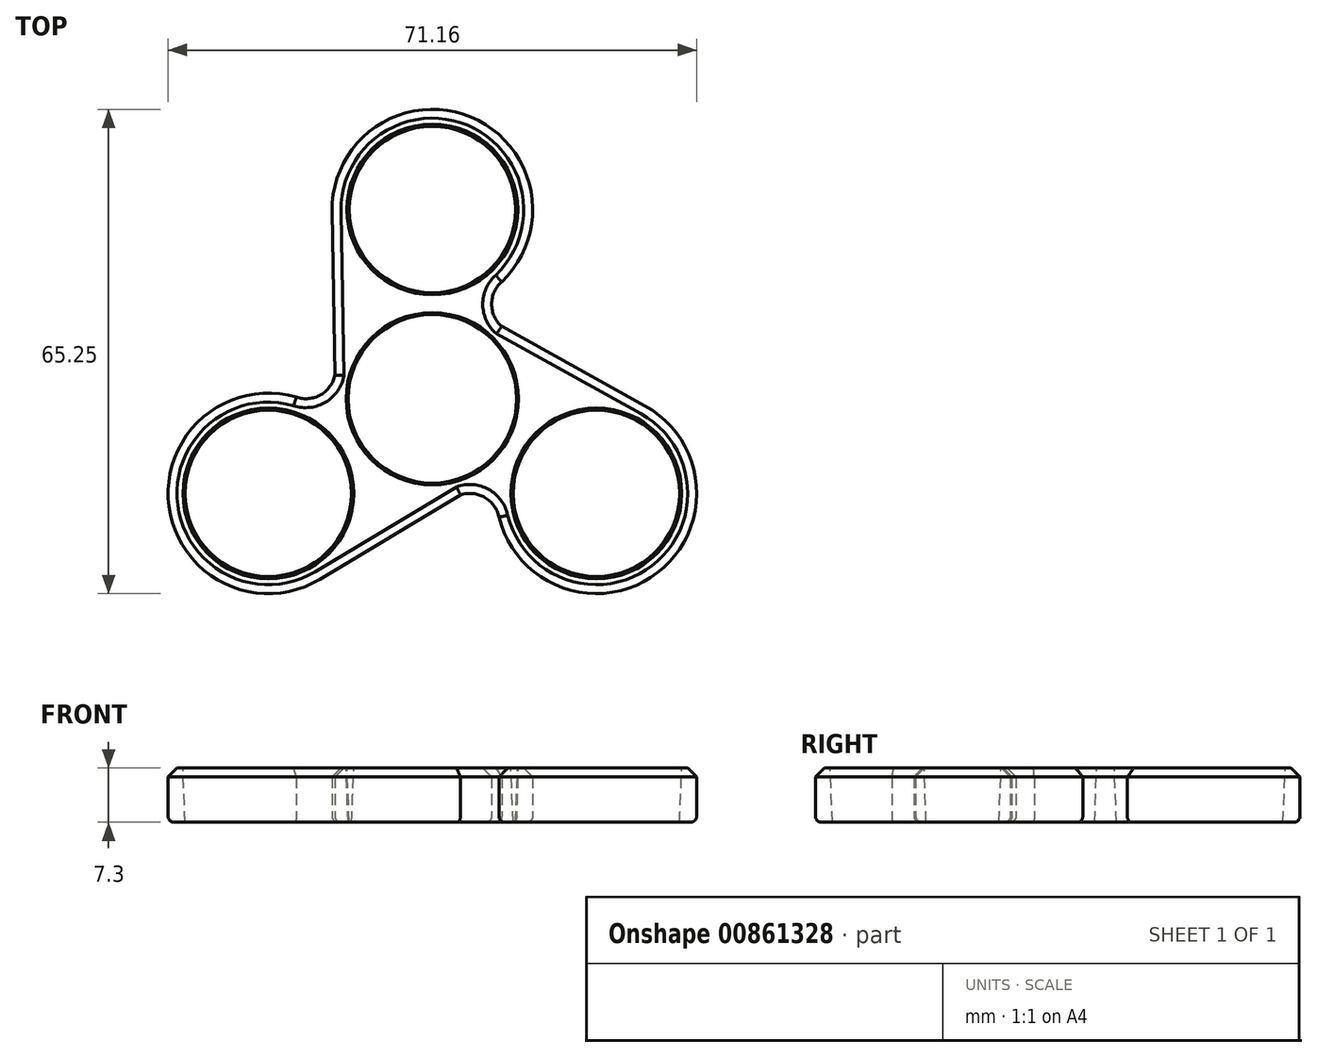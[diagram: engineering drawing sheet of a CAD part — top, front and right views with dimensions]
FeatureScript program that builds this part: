
annotation { "Feature Type Name" : "Feature", "Feature Type Description" : "" }
export const myFeature = defineFeature(function(context is Context, id is Id, definition is map)
    precondition{}
    {
        {
            var Q0;
            Q0=qCreatedBy(makeId("Top.planeOp"),FACE);
            var sketch = newSketch(context, id + "F0", { "sketchPlane" : qUnion([Q0])});
            skCircle(sketch, "E0", {"center": v(0, 0) * mm, "radius": 13.5 * mm});
            skCircle(sketch, "E1", {"center": v(0, 25.5) * mm, "radius": 13.5 * mm});
            skLineSegment(sketch, "E2.bottom", {"start": v(0, 9.75) * mm, "end": v(9.34, 9.75) * mm});
            skLineSegment(sketch, "E2.top", {"start": v(0, 15.75) * mm, "end": v(9.34, 15.75) * mm});
            skLineSegment(sketch, "E2.left", {"start": v(0, 9.75) * mm, "end": v(0, 15.75) * mm});
            skLineSegment(sketch, "E2.right", {"start": v(9.34, 9.75) * mm, "end": v(9.34, 15.75) * mm});
            skArc(sketch, "E3", {"start": v(9.34, 15.75) * mm, "mid": v(7.98, 12.75) * mm, "end": v(9.34, 9.75) * mm});
            skArc(sketch, "E4.1.0", {"start": v(-18.3, 0.21) * mm, "mid": v(-15.03, 0.54) * mm, "end": v(-13.11, 3.21) * mm});
            skCircle(sketch, "E4.1.1", {"center": v(-22.08, -12.75) * mm, "radius": 13.5 * mm});
            skArc(sketch, "E4.2.0", {"start": v(8.97, -15.96) * mm, "mid": v(7.05, -13.29) * mm, "end": v(3.78, -12.96) * mm});
            skCircle(sketch, "E4.2.1", {"center": v(22.08, -12.75) * mm, "radius": 13.5 * mm});
            skLineSegment(sketch, "E5", {"start": v(9.34, 9.75) * mm, "end": v(28.63, -0.94) * mm});
            skLineSegment(sketch, "E6.1.0", {"start": v(-13.11, 3.21) * mm, "end": v(-13.5, 25.26) * mm});
            skLineSegment(sketch, "E6.2.0", {"start": v(3.78, -12.96) * mm, "end": v(-15.13, -24.32) * mm});
            skSolve(sketch);
        }
        {
            var Q0;
            {var subQ0=sQuery(id+"F0.wireOp",EDGE,"E2.top");Q0=makeQuery(id+"F0.imprint","IMPRINT",FACE,{"disambiguationData":[TD([[makeQuery(id+"F0.imprint","IMPRINT",EDGE,{"derivedFrom":subQ0}),1.0]])]});}
            var Q1;
            {var subQ0=sQuery(id+"F0.wireOp",EDGE,"E6.1.0");Q1=makeQuery(id+"F0.imprint","IMPRINT",FACE,{"disambiguationData":[TD([[makeQuery(id+"F0.imprint","IMPRINT",EDGE,{"derivedFrom":subQ0}),-1.0]])]});}
            var Q2;
            {var subQ1=sQuery(id+"F0.wireOp",EDGE,"E2.top");Q2=makeQuery(id+"F0.imprint","IMPRINT",FACE,{"disambiguationData":[TD([[makeQuery(id+"F0.imprint","IMPRINT",EDGE,{"derivedFrom":subQ1}),-1.0]])]});}
            var Q3;
            {var subQ0=sQuery(id+"F0.wireOp",EDGE,"E1");var subQ1=sQuery(id+"F0.wireOp",EDGE,"E0");var subQ2=makeQuery(id+"F0.imprint","INTERSECT",VERTEX,{"disambiguationData":[OD(0.0)],"derivedFrom":[subQ1,subQ0]});Q3=makeQuery(id+"F0.imprint","IMPRINT",FACE,{"disambiguationData":[TD([[makeQuery(id+"F0.imprint","IMPRINT",EDGE,{"disambiguationData":[TD([[subQ2,-1.0]])],"derivedFrom":subQ1}),1.0]])]});}
            var Q4;
            {var subQ0=sQuery(id+"F0.wireOp",EDGE,"E2.left");var subQ1=sQuery(id+"F0.wireOp",EDGE,"E0");var subQ2=makeQuery(id+"F0.imprint","INTERSECT",VERTEX,{"derivedFrom":[subQ1,subQ0]});Q4=makeQuery(id+"F0.imprint","IMPRINT",FACE,{"disambiguationData":[TD([[makeQuery(id+"F0.imprint","IMPRINT",EDGE,{"disambiguationData":[TD([[subQ2,-1.0]])],"derivedFrom":subQ1}),1.0]])]});}
            var Q5;
            {var subQ5=sQuery(id+"F0.wireOp",EDGE,"E2.bottom");Q5=makeQuery(id+"F0.imprint","IMPRINT",FACE,{"disambiguationData":[TD([[makeQuery(id+"F0.imprint","IMPRINT",EDGE,{"derivedFrom":subQ5}),-1.0]])]});}
            var Q6;
            {var subQ0=sQuery(id+"F0.wireOp",EDGE,"E3");var subQ1=sQuery(id+"F0.wireOp",EDGE,"E0");var subQ2=makeQuery(id+"F0.imprint","INTERSECT",VERTEX,{"derivedFrom":[subQ1,subQ0]});Q6=makeQuery(id+"F0.imprint","IMPRINT",FACE,{"disambiguationData":[TD([[makeQuery(id+"F0.imprint","IMPRINT",EDGE,{"disambiguationData":[TD([[subQ2,-1.0]])],"derivedFrom":subQ1}),-1.0]])]});}
            var Q7;
            {var subQ0=sQuery(id+"F0.wireOp",EDGE,"E2.bottom");Q7=makeQuery(id+"F0.imprint","IMPRINT",FACE,{"disambiguationData":[TD([[makeQuery(id+"F0.imprint","IMPRINT",EDGE,{"derivedFrom":subQ0}),1.0]])]});}
            var Q8;
            {var subQ0=sQuery(id+"F0.wireOp",EDGE,"E4.2.1");var subQ1=sQuery(id+"F0.wireOp",EDGE,"E0");var subQ2=makeQuery(id+"F0.imprint","INTERSECT",VERTEX,{"disambiguationData":[OD(0.0)],"derivedFrom":[subQ1,subQ0]});Q8=makeQuery(id+"F0.imprint","IMPRINT",FACE,{"disambiguationData":[TD([[makeQuery(id+"F0.imprint","IMPRINT",EDGE,{"disambiguationData":[TD([[subQ2,-1.0]])],"derivedFrom":subQ1}),1.0]])]});}
            var Q9;
            {var subQ0=sQuery(id+"F0.wireOp",EDGE,"E4.2.0");var subQ1=sQuery(id+"F0.wireOp",EDGE,"E0");var subQ2=makeQuery(id+"F0.imprint","INTERSECT",VERTEX,{"derivedFrom":[subQ1,subQ0]});Q9=makeQuery(id+"F0.imprint","IMPRINT",FACE,{"disambiguationData":[TD([[makeQuery(id+"F0.imprint","IMPRINT",EDGE,{"disambiguationData":[TD([[subQ2,-1.0]])],"derivedFrom":subQ1}),-1.0]])]});}
            var Q10;
            {var subQ0=sQuery(id+"F0.wireOp",EDGE,"E6.2.0");Q10=makeQuery(id+"F0.imprint","IMPRINT",FACE,{"disambiguationData":[TD([[makeQuery(id+"F0.imprint","IMPRINT",EDGE,{"derivedFrom":subQ0}),-1.0]])]});}
            var Q11;
            {var subQ0=sQuery(id+"F0.wireOp",EDGE,"E4.1.1");var subQ1=sQuery(id+"F0.wireOp",EDGE,"E0");var subQ2=makeQuery(id+"F0.imprint","INTERSECT",VERTEX,{"disambiguationData":[OD(0.0)],"derivedFrom":[subQ1,subQ0]});Q11=makeQuery(id+"F0.imprint","IMPRINT",FACE,{"disambiguationData":[TD([[makeQuery(id+"F0.imprint","IMPRINT",EDGE,{"disambiguationData":[TD([[subQ2,-1.0]])],"derivedFrom":subQ1}),1.0]])]});}
            var Q12;
            {var subQ0=sQuery(id+"F0.wireOp",EDGE,"E4.1.0");var subQ1=sQuery(id+"F0.wireOp",EDGE,"E0");var subQ2=makeQuery(id+"F0.imprint","INTERSECT",VERTEX,{"derivedFrom":[subQ1,subQ0]});Q12=makeQuery(id+"F0.imprint","IMPRINT",FACE,{"disambiguationData":[TD([[makeQuery(id+"F0.imprint","IMPRINT",EDGE,{"disambiguationData":[TD([[subQ2,-1.0]])],"derivedFrom":subQ1}),-1.0]])]});}
            var Q13;
            {var subQ0=sQuery(id+"F0.wireOp",EDGE,"E4.1.1");var subQ2=sQuery(id+"F0.wireOp",EDGE,"E0");var subQ6=makeQuery(id+"F0.imprint","INTERSECT",VERTEX,{"disambiguationData":[OD(0.0)],"derivedFrom":[subQ2,subQ0]});Q13=makeQuery(id+"F0.imprint","IMPRINT",FACE,{"disambiguationData":[TD([[makeQuery(id+"F0.imprint","IMPRINT",EDGE,{"disambiguationData":[TD([[subQ6,-1.0]])],"derivedFrom":subQ2}),-1.0]])]});}
            var Q14;
            {var subQ0=sQuery(id+"F0.wireOp",EDGE,"E4.2.1");var subQ2=sQuery(id+"F0.wireOp",EDGE,"E0");var subQ6=makeQuery(id+"F0.imprint","INTERSECT",VERTEX,{"disambiguationData":[OD(0.0)],"derivedFrom":[subQ2,subQ0]});Q14=makeQuery(id+"F0.imprint","IMPRINT",FACE,{"disambiguationData":[TD([[makeQuery(id+"F0.imprint","IMPRINT",EDGE,{"disambiguationData":[TD([[subQ6,-1.0]])],"derivedFrom":subQ2}),-1.0]])]});}
            var Q15;
            {var subQ0=sQuery(id+"F0.wireOp",EDGE,"E5");Q15=makeQuery(id+"F0.imprint","IMPRINT",FACE,{"disambiguationData":[TD([[makeQuery(id+"F0.imprint","IMPRINT",EDGE,{"derivedFrom":subQ0}),-1.0]])]});}
            extrude(context, id + "F1", {"entities" : qUnion([Q0, Q1, Q2, Q3, Q4, Q5, Q6, Q7, Q8, Q9, Q10, Q11, Q12, Q13, Q14, Q15]), "depth" : 7.3 * mm, "offsetDistance" : 25 * mm});
        }
        {
            var Q0;
            Q0=makeQuery(id+"F1.opExtrude","CAP_FACE",FACE,{"disambiguationData":[OSD([sQuery(id+"F0.wireOp",EDGE,"E1"),sQuery(id+"F0.wireOp",EDGE,"E3"),sQuery(id+"F0.wireOp",EDGE,"E4.1.0"),sQuery(id+"F0.wireOp",EDGE,"E4.1.1"),sQuery(id+"F0.wireOp",EDGE,"E4.2.0"),sQuery(id+"F0.wireOp",EDGE,"E4.2.1"),sQuery(id+"F0.wireOp",EDGE,"E5"),sQuery(id+"F0.wireOp",EDGE,"E6.1.0"),sQuery(id+"F0.wireOp",EDGE,"E6.2.0")])],"isStart":true});
            fillet(context, id + "F2", {"entities" : qUnion([Q0]), "radius" : 0.8 * mm, "tangentPropagation" : true, "allowEdgeOverflow" : false});
        }
        {
            var Q0;
            Q0=makeQuery(id+"F1.opExtrude","CAP_FACE",FACE,{"disambiguationData":[OSD([sQuery(id+"F0.wireOp",EDGE,"E1"),sQuery(id+"F0.wireOp",EDGE,"E3"),sQuery(id+"F0.wireOp",EDGE,"E4.1.0"),sQuery(id+"F0.wireOp",EDGE,"E4.1.1"),sQuery(id+"F0.wireOp",EDGE,"E4.2.0"),sQuery(id+"F0.wireOp",EDGE,"E4.2.1"),sQuery(id+"F0.wireOp",EDGE,"E5"),sQuery(id+"F0.wireOp",EDGE,"E6.1.0"),sQuery(id+"F0.wireOp",EDGE,"E6.2.0")])],"isStart":false});
            chamfer(context, id + "F3", {"entities" : qUnion([Q0]), "width" : 1.2 * mm, "tangentPropagation" : true});
        }
        {
            var Q0;
            Q0=makeQuery(id+"F1.opExtrude","CAP_FACE",FACE,{"disambiguationData":[OSD([sQuery(id+"F0.wireOp",EDGE,"E1"),sQuery(id+"F0.wireOp",EDGE,"E3"),sQuery(id+"F0.wireOp",EDGE,"E4.1.0"),sQuery(id+"F0.wireOp",EDGE,"E4.1.1"),sQuery(id+"F0.wireOp",EDGE,"E4.2.0"),sQuery(id+"F0.wireOp",EDGE,"E4.2.1"),sQuery(id+"F0.wireOp",EDGE,"E5"),sQuery(id+"F0.wireOp",EDGE,"E6.1.0"),sQuery(id+"F0.wireOp",EDGE,"E6.2.0")])],"isStart":false});
            var sketch = newSketch(context, id + "F4", { "sketchPlane" : qUnion([Q0])});
            skCircle(sketch, "E7", {"center": v(0, 0) * mm, "radius": 11.6 * mm});
            skCircle(sketch, "E8", {"center": v(0, 25.5) * mm, "radius": 11.5 * mm});
            skCircle(sketch, "E9.1.0", {"center": v(-22.08, -12.75) * mm, "radius": 11.5 * mm});
            skCircle(sketch, "E9.2.0", {"center": v(22.08, -12.75) * mm, "radius": 11.5 * mm});
            skSolve(sketch);
        }
        {
            var Q0;
            Q0=makeQuery(id+"F1.opExtrude","CAP_FACE",FACE,{"disambiguationData":[OSD([sQuery(id+"F0.wireOp",EDGE,"E1"),sQuery(id+"F0.wireOp",EDGE,"E3"),sQuery(id+"F0.wireOp",EDGE,"E4.1.0"),sQuery(id+"F0.wireOp",EDGE,"E4.1.1"),sQuery(id+"F0.wireOp",EDGE,"E4.2.0"),sQuery(id+"F0.wireOp",EDGE,"E4.2.1"),sQuery(id+"F0.wireOp",EDGE,"E5"),sQuery(id+"F0.wireOp",EDGE,"E6.1.0"),sQuery(id+"F0.wireOp",EDGE,"E6.2.0")])],"isStart":true});
            var sketch = newSketch(context, id + "F5", { "sketchPlane" : qUnion([Q0])});
            skCircle(sketch, "E10", {"center": v(0, 0) * mm, "radius": 11.35 * mm});
            skCircle(sketch, "E11", {"center": v(-22.08, 12.75) * mm, "radius": 11.2 * mm});
            skCircle(sketch, "E12.1.0", {"center": v(0, -25.5) * mm, "radius": 11.2 * mm});
            skCircle(sketch, "E12.2.0", {"center": v(22.08, 12.75) * mm, "radius": 11.2 * mm});
            skSolve(sketch);
        }
        {
            var Q1;
            Q1=makeQuery(id+"F4.imprint","IMPRINT",FACE,{"disambiguationData":[TD([[makeQuery(id+"F4.imprint","IMPRINT",EDGE,{"derivedFrom":sQuery(id+"F4.wireOp",EDGE,"E7")}),1.0]])]});
            var Q2;
            Q2=makeQuery(id+"F5.imprint","IMPRINT",FACE,{"disambiguationData":[TD([[makeQuery(id+"F5.imprint","IMPRINT",EDGE,{"derivedFrom":sQuery(id+"F5.wireOp",EDGE,"E10")}),1.0]])]});
            loft(context, id + "F6", {"operationType" : NewBodyOperationType.REMOVE, "sheetProfilesArray" : [{ "sheetProfileEntities" : qUnion([Q1]) }, { "sheetProfileEntities" : qUnion([Q2]) }]});
        }
        {
            var Q1;
            Q1=makeQuery(id+"F4.imprint","IMPRINT",FACE,{"disambiguationData":[TD([[makeQuery(id+"F4.imprint","IMPRINT",EDGE,{"derivedFrom":sQuery(id+"F4.wireOp",EDGE,"E9.2.0")}),1.0]])]});
            var Q2;
            Q2=makeQuery(id+"F5.imprint","IMPRINT",FACE,{"disambiguationData":[TD([[makeQuery(id+"F5.imprint","IMPRINT",EDGE,{"derivedFrom":sQuery(id+"F5.wireOp",EDGE,"E12.2.0")}),1.0]])]});
            loft(context, id + "F7", {"operationType" : NewBodyOperationType.REMOVE, "sheetProfilesArray" : [{ "sheetProfileEntities" : qUnion([Q1]) }, { "sheetProfileEntities" : qUnion([Q2]) }]});
        }
        {
            var Q1;
            Q1=makeQuery(id+"F4.imprint","IMPRINT",FACE,{"disambiguationData":[TD([[makeQuery(id+"F4.imprint","IMPRINT",EDGE,{"derivedFrom":sQuery(id+"F4.wireOp",EDGE,"E8")}),1.0]])]});
            var Q2;
            Q2=makeQuery(id+"F5.imprint","IMPRINT",FACE,{"disambiguationData":[TD([[makeQuery(id+"F5.imprint","IMPRINT",EDGE,{"derivedFrom":sQuery(id+"F5.wireOp",EDGE,"E12.1.0")}),1.0]])]});
            loft(context, id + "F8", {"operationType" : NewBodyOperationType.REMOVE, "sheetProfilesArray" : [{ "sheetProfileEntities" : qUnion([Q1]) }, { "sheetProfileEntities" : qUnion([Q2]) }]});
        }
        {
            var Q1;
            Q1=makeQuery(id+"F4.imprint","IMPRINT",FACE,{"disambiguationData":[TD([[makeQuery(id+"F4.imprint","IMPRINT",EDGE,{"derivedFrom":sQuery(id+"F4.wireOp",EDGE,"E9.1.0")}),1.0]])]});
            var Q2;
            Q2=makeQuery(id+"F5.imprint","IMPRINT",FACE,{"disambiguationData":[TD([[makeQuery(id+"F5.imprint","IMPRINT",EDGE,{"derivedFrom":sQuery(id+"F5.wireOp",EDGE,"E11")}),1.0]])]});
            loft(context, id + "F9", {"operationType" : NewBodyOperationType.REMOVE, "sheetProfilesArray" : [{ "sheetProfileEntities" : qUnion([Q1]) }, { "sheetProfileEntities" : qUnion([Q2]) }]});
        }
    });
